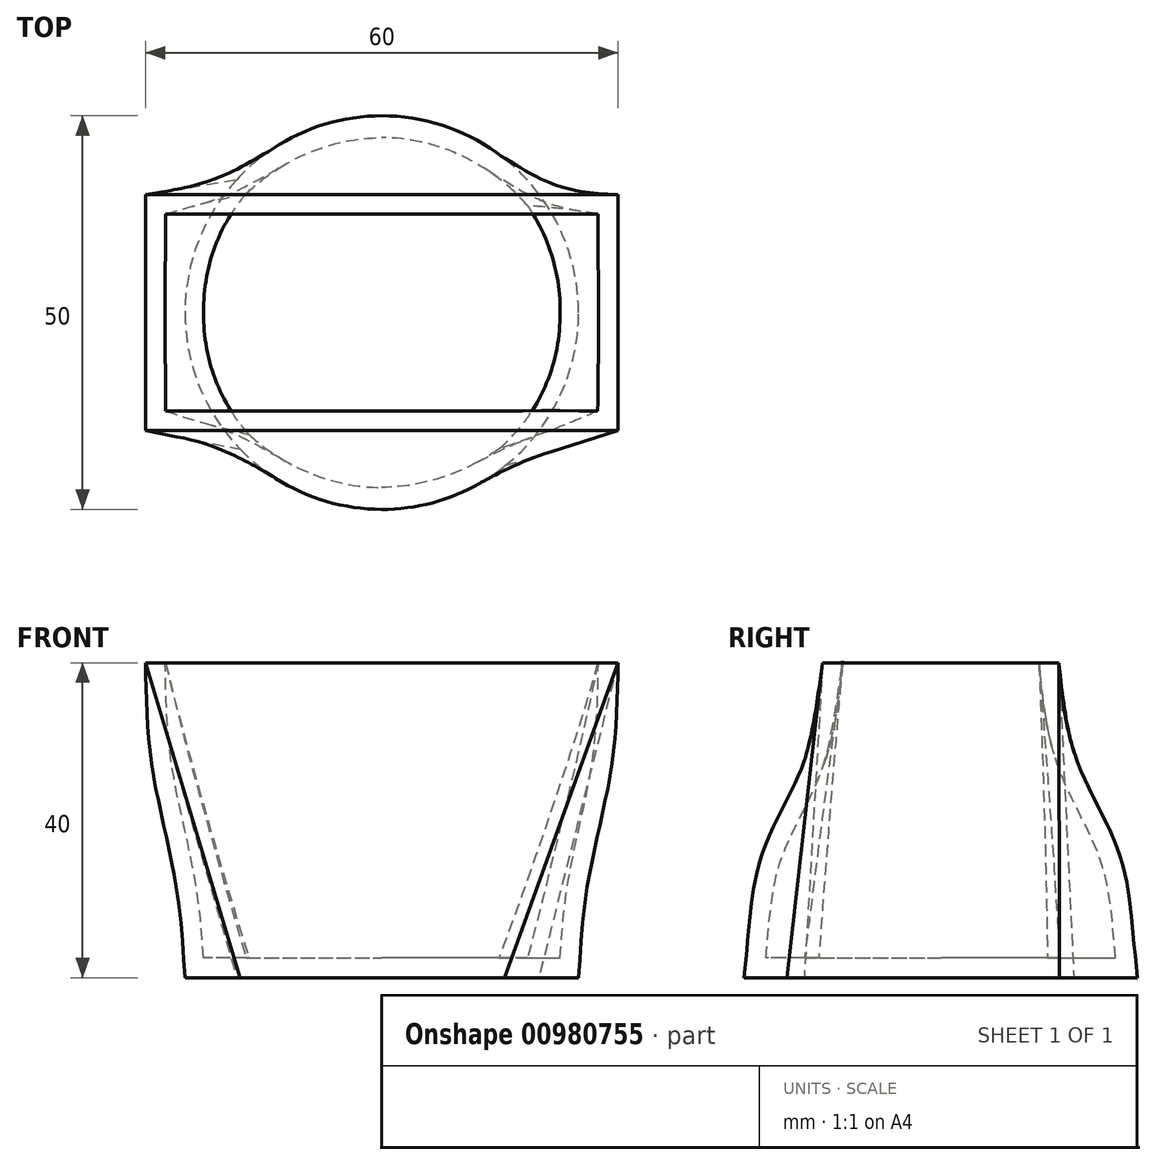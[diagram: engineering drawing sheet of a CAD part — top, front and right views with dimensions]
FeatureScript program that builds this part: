
annotation { "Feature Type Name" : "Feature", "Feature Type Description" : "" }
export const myFeature = defineFeature(function(context is Context, id is Id, definition is map)
    precondition{}
    {
        {
            var Q0;
            Q0=qCreatedBy(makeId("Top.planeOp"),FACE);
            var sketch = newSketch(context, id + "F0", { "sketchPlane" : qUnion([Q0])});
            skArc(sketch, "E0", {"start": v(-18.41, 16.9) * mm, "mid": v(-25, -0.3) * mm, "end": v(-18, -17.34) * mm});
            skArc(sketch, "E1", {"start": v(19.94, 15.08) * mm, "mid": v(1.2, 24.97) * mm, "end": v(-18.41, 16.9) * mm});
            skArc(sketch, "E2", {"start": v(15.62, -19.52) * mm, "mid": v(24.8, -3.1) * mm, "end": v(19.94, 15.08) * mm});
            skArc(sketch, "E3", {"start": v(-18, -17.34) * mm, "mid": v(-1.61, -24.95) * mm, "end": v(15.62, -19.52) * mm});
            skSolve(sketch);
        }
        {
            var Q0;
            Q0=qCreatedBy(makeId("Top.planeOp"),FACE);
            cPlane(context, id + "F1", {"entities" : qUnion([Q0]), "cplaneType" : CPlaneType.OFFSET, "offset" : 40 * mm, "width" : 150 * mm, "height" : 150 * mm});
        }
        {
            var Q0;
            Q0=qCreatedBy(id+"F1.planeOp",FACE);
            var sketch = newSketch(context, id + "F2", { "sketchPlane" : qUnion([Q0])});
            skLineSegment(sketch, "E4.bottom", {"start": v(30, -15) * mm, "end": v(-30, -15) * mm});
            skLineSegment(sketch, "E4.top", {"start": v(30, 15) * mm, "end": v(-30, 15) * mm});
            skLineSegment(sketch, "E4.left", {"start": v(30, -15) * mm, "end": v(30, 15) * mm});
            skLineSegment(sketch, "E4.right", {"start": v(-30, -15) * mm, "end": v(-30, 15) * mm});
            skPoint(sketch, "E4.middle", {"position": v(0, 0) * mm});
            skSolve(sketch);
        }
        {
            var Q0;
            Q0=qCreatedBy(makeId("Front.planeOp"),FACE);
            var sketch = newSketch(context, id + "F3", { "sketchPlane" : qUnion([Q0])});
            skLineSegment(sketch, "E5", {"start": v(0, 0) * mm, "end": v(0, 33.4) * mm, "construction": true});
            skFitSpline(sketch, "E6", {"points": [v(-30, 40) * mm, v(-28.42, 22.67) * mm, v(-25.88, 10.12) * mm, v(-25, 0) * mm], "startDerivative": vector(0.5, -69.9) * mm, "endDerivative": vector(2.46, -32.7) * mm});
            skFitSpline(sketch, "E7.MirrorCS", {"points": [v(30, 40) * mm, v(28.42, 22.67) * mm, v(25.88, 10.12) * mm, v(25, 0) * mm], "startDerivative": vector(-0.5, -69.9) * mm, "endDerivative": vector(-2.46, -32.7) * mm});
            skSolve(sketch);
        }
        {
            var Q0;
            Q0=qCreatedBy(makeId("Right.planeOp"),FACE);
            var sketch = newSketch(context, id + "F4", { "sketchPlane" : qUnion([Q0])});
            skFitSpline(sketch, "E8", {"points": [v(15, 40) * mm, v(17.55, 26.93) * mm, v(22.97, 14.81) * mm, v(25, 0) * mm], "startDerivative": vector(1.52, -37.39) * mm, "endDerivative": vector(5.16, -39.88) * mm});
            skFitSpline(sketch, "E9.MirrorCS", {"points": [v(-15, 40) * mm, v(-17.55, 26.93) * mm, v(-22.97, 14.81) * mm, v(-25, 0) * mm], "startDerivative": vector(-1.52, -37.39) * mm, "endDerivative": vector(-5.16, -39.88) * mm});
            skSolve(sketch);
        }
        {
            var Q0;
            Q0=makeQuery(id+"F2.imprint","IMPRINT",FACE,{"disambiguationData":[TD([[makeQuery(id+"F2.imprint","IMPRINT",EDGE,{"derivedFrom":sQuery(id+"F2.wireOp",EDGE,"E4.bottom")}),-1.0]])]});
            var Q1;
            Q1=makeQuery(id+"F0.imprint","IMPRINT",FACE,{"disambiguationData":[TD([[makeQuery(id+"F0.imprint","IMPRINT",EDGE,{"derivedFrom":sQuery(id+"F0.wireOp",EDGE,"E0")}),1.0]])]});
            var Q2;
            Q2=sQuery(id+"F3.wireOp",EDGE,"E7.MirrorCS");
            var Q3;
            Q3=sQuery(id+"F3.wireOp",EDGE,"E6");
            var Q4;
            Q4=sQuery(id+"F4.wireOp",EDGE,"E9.MirrorCS");
            var Q5;
            Q5=sQuery(id+"F4.wireOp",EDGE,"E8");
            loft(context, id + "F5", {"addGuides" : true, "sheetProfilesArray" : [{ "sheetProfileEntities" : qUnion([Q0]) }, { "sheetProfileEntities" : qUnion([Q1]) }], "guidesArray" : [{ "guideEntities" : qUnion([Q2]), "guideDerivativeType" : LoftGuideDerivativeType.DEFAULT, "guideDerivativeMagnitude" : 1 }, { "guideEntities" : qUnion([Q3]), "guideDerivativeType" : LoftGuideDerivativeType.DEFAULT, "guideDerivativeMagnitude" : 1 }, { "guideEntities" : qUnion([Q4]), "guideDerivativeType" : LoftGuideDerivativeType.DEFAULT, "guideDerivativeMagnitude" : 1 }, { "guideEntities" : qUnion([Q5]), "guideDerivativeType" : LoftGuideDerivativeType.DEFAULT, "guideDerivativeMagnitude" : 1 }]});
        }
        {
            var Q0;
            Q0=makeQuery(id+"F5.opLoft","CAP_FACE",FACE,{"disambiguationData":[OSD([makeQuery(id+"F2.imprint","IMPRINT",FACE,{"disambiguationData":[TD([[makeQuery(id+"F2.imprint","IMPRINT",EDGE,{"derivedFrom":sQuery(id+"F2.wireOp",EDGE,"E4.bottom")}),-1.0]])]})])],"isStart":true});
            var Q1;
            Q1=makeQuery(id+"F5.opLoft","CAP_FACE",FACE,{"disambiguationData":[OSD([makeQuery(id+"F0.imprint","IMPRINT",FACE,{"disambiguationData":[TD([[makeQuery(id+"F0.imprint","IMPRINT",EDGE,{"derivedFrom":sQuery(id+"F0.wireOp",EDGE,"E0")}),1.0]])]})])],"isStart":true});
            shell(context, id + "F6", {"entities" : qUnion([Q0, Q1]), "thickness" : 2.5 * mm});
        }
    });
